SOLIDWORKS PART (.sldprt)
format: sldprt  version: not decoded by parser v0  size: 280,576 bytes
history: native  units: mm
features: sketch x17, extrude x8, cut_extrude x5, plane x4, chamfer x2, mirror x1 + 1 further entry (+9 scaffold rows collapsed)
feature tree (47):
  "Annotations"  RD1=4.445mm RD3=2mm
  scaffold x9  (default folders/planes/origin — collapsed)
  sketch  "Sketch1"  dims[c1.D3=2.5mm c1.D4=5.0mm c1.D6=2.5mm c1.D1=41.8mm c1.D2=22.7mm c2.D4=~40.298183mm c2.D5=21.2mm]
  extrude  "Base-Extrude"  Depth=13.7mm
  sketch  "Sketch2"  dims[c1.D1=~4.28035mm c1.D2=9.271mm c1.D3=1.75mm c1.D4=3.5mm c2.D1=15.6mm c2.D4=~11.04392mm]
  extrude  "Boss-Extrude1"  Depth=0.55mm
  sketch  "Sketch3"  dims[D1=7.0mm D2=1.5mm]
  extrude  "Boss-Extrude2"  Depth=9.2456mm
  plane  "Plane1"  Offset=8.1534mm
  sketch  "Sketch5"  dims[D1=3.5mm D2=~3.475551mm]
  cut_extrude  "Cut-Extrude1"  [1 undecoded]
  sketch  "Sketch6"  dims[c1.D1=~1.372138mm c1.D2=3.937mm c2.D1=24.257mm]
  extrude  "Boss-Extrude3"  Depth=2mm
  plane  "Backside Plane"  Offset=0mm
  sketch  "Sketch8"
  plane  "Middle Plane"
  sketch  "Sketch11"  dims[c1.D1=7.2mm c1.D2=9.779mm c1.D3=6.985mm c2.D1=~11.04392mm]
  extrude  "Boss-Extrude4"  Depth=2.921mm
  sketch  "Sketch12"  dims[D1=~6.374291mm]
  extrude  "Boss-Extrude5"  Depth=8.94mm
  sketch  "Sketch13"  dims[D1=~2.730872mm]
  sketch  "Sketch14"  dims[D1=3.5179mm]
  cut_extrude  "Cut-Extrude2"  Depth=12.1mm
  sketch  "Sketch15"  dims[c1.D2=~12.270569mm c1.D1=17.4mm c2.D1=15.66mm c2.D5=1.15mm c2.D6=1.0mm c2.D7=5.0mm]
  sketch  "Sketch16"  dims[c1.D1=~1.040407mm c1.D2=~0.973054mm c1.D5=2.0mm c2.D2=2.286mm c2.D1=5.334mm c3.D2=3.3mm c3.D3=4.572mm c3.D4=11.35mm c3.D5=11.35mm c3.D1=5.205mm c4.D2=3.3mm c4.D3=3.3mm c4.D4=3.3mm c5.D2=3.175mm]
  extrude  "Boss-Extrude7"  Depth=5.08mm
  sketch  "Sketch18"
  plane  "Plane5"
  mirror  "Mirror2"
  sketch  "Sketch33"
  sketch  "Sketch34"
  extrude  "Extrude1"  Depth=4.445mm
  sketch  "Sketch35"  dims[D1=6.096mm D2=11.35mm D3=7.55mm D4=7.55mm]
  cut_extrude  "Cut-Extrude4"  Depth=14.445mm
  cut_extrude  "Cut-Extrude5"  Depth=10mm
  chamfer  "Chamfer1"  Distance=0.25mm Angle=45deg
  chamfer  "Chamfer2"  Distance=0.25mm Angle=45deg
  sketch  "Sketch36"  dims[c1.D1=3.5mm c1.D2=3.5mm c2.D1=3.5mm c2.D2=~0.070127mm]
  cut_extrude  "Cut-Extrude6"  Depth=1.525mm Thickness=1.21mm
decode coverage: 27 of 33 modeling features carry decoded parameters; 1 rows unclassified (native names shown)
note: ~ marks probable driven/reference dimensions
note: 1 parameter value undecoded
note: suppression state not decoded; provenance and decode notes live in map.json
